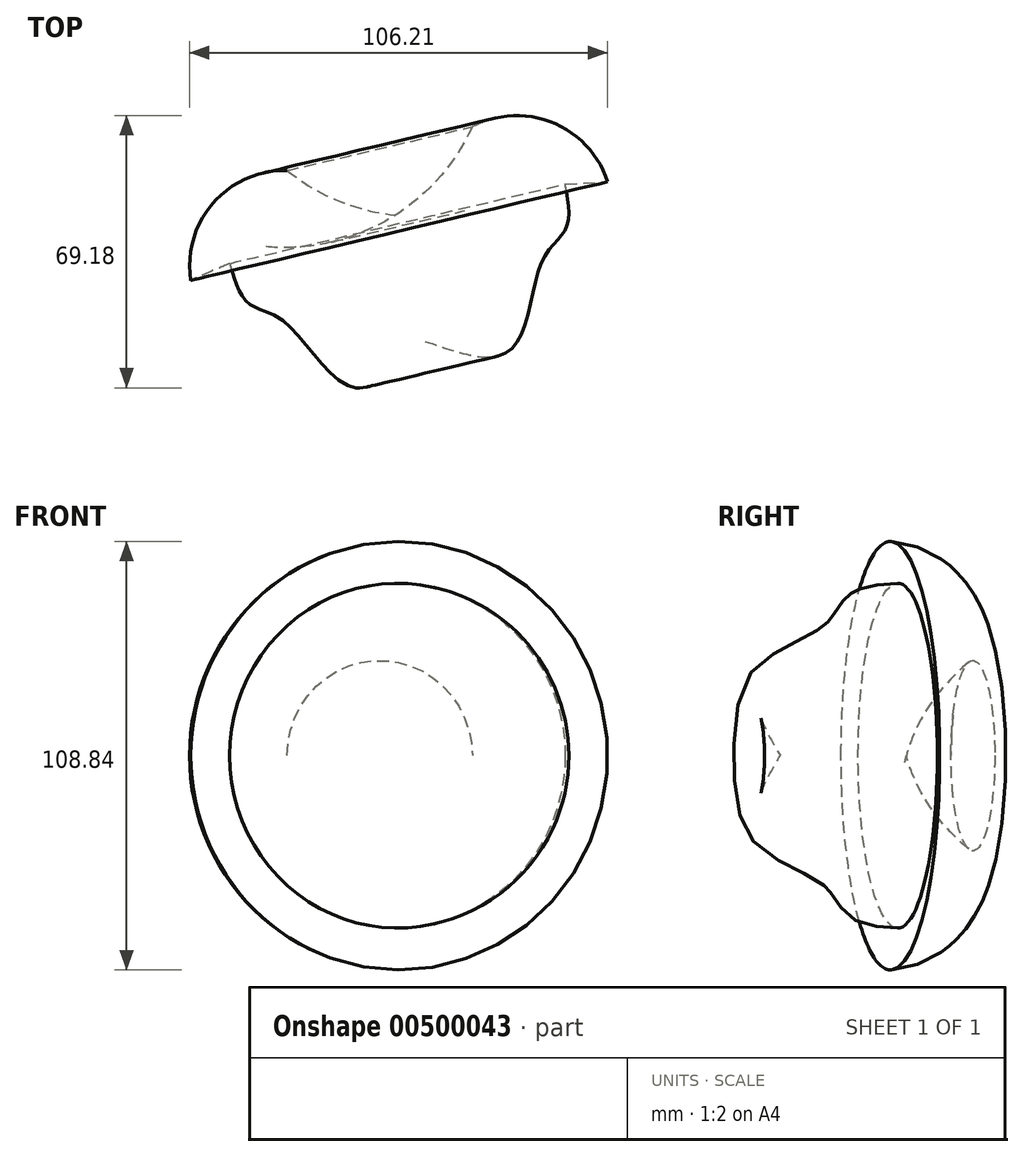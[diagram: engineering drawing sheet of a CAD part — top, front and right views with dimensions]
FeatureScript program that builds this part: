
annotation { "Feature Type Name" : "Feature", "Feature Type Description" : "" }
export const myFeature = defineFeature(function(context is Context, id is Id, definition is map)
    precondition{}
    {
        {
            var Q0;
            Q0=qCreatedBy(makeId("Top.planeOp"),FACE);
            var sketch = newSketch(context, id + "F0", { "sketchPlane" : qUnion([Q0])});
            skArc(sketch, "E0", {"start": v(34.4, 22.59) * mm, "mid": v(20.46, 37.62) * mm, "end": v(0, 36.58) * mm});
            skArc(sketch, "E1", {"start": v(-19.53, 14.14) * mm, "mid": v(-8.14, 23.95) * mm, "end": v(0, 36.58) * mm});
            skLineSegment(sketch, "E2", {"start": v(-19.53, 14.14) * mm, "end": v(-11.95, -17.93) * mm});
            skFitSpline(sketch, "E3", {"points": [v(-11.95, -17.93) * mm, v(9.91, -19.97) * mm, v(17.78, 2.48) * mm, v(23.9, 10.93) * mm, v(23.6, 22) * mm], "startDerivative": vector(89.37, -31.6) * mm, "endDerivative": vector(-10.96, 59.76) * mm});
            skLineSegment(sketch, "E4", {"start": v(23.6, 22) * mm, "end": v(34.4, 22.59) * mm});
            skSolve(sketch);
        }
        {
            var Q0;
            Q0=makeQuery(id+"F0.imprint","IMPRINT",FACE,{"disambiguationData":[TD([[makeQuery(id+"F0.imprint","IMPRINT",EDGE,{"derivedFrom":sQuery(id+"F0.wireOp",EDGE,"E0")}),1.0]])]});
            var Q1;
            Q1=sQuery(id+"F0.wireOp",EDGE,"E2");
            revolve(context, id + "F1", {"entities" : qUnion([Q0]), "axis" : qUnion([Q1]), "revolveType" : RevolveType.FULL});
        }
    });
